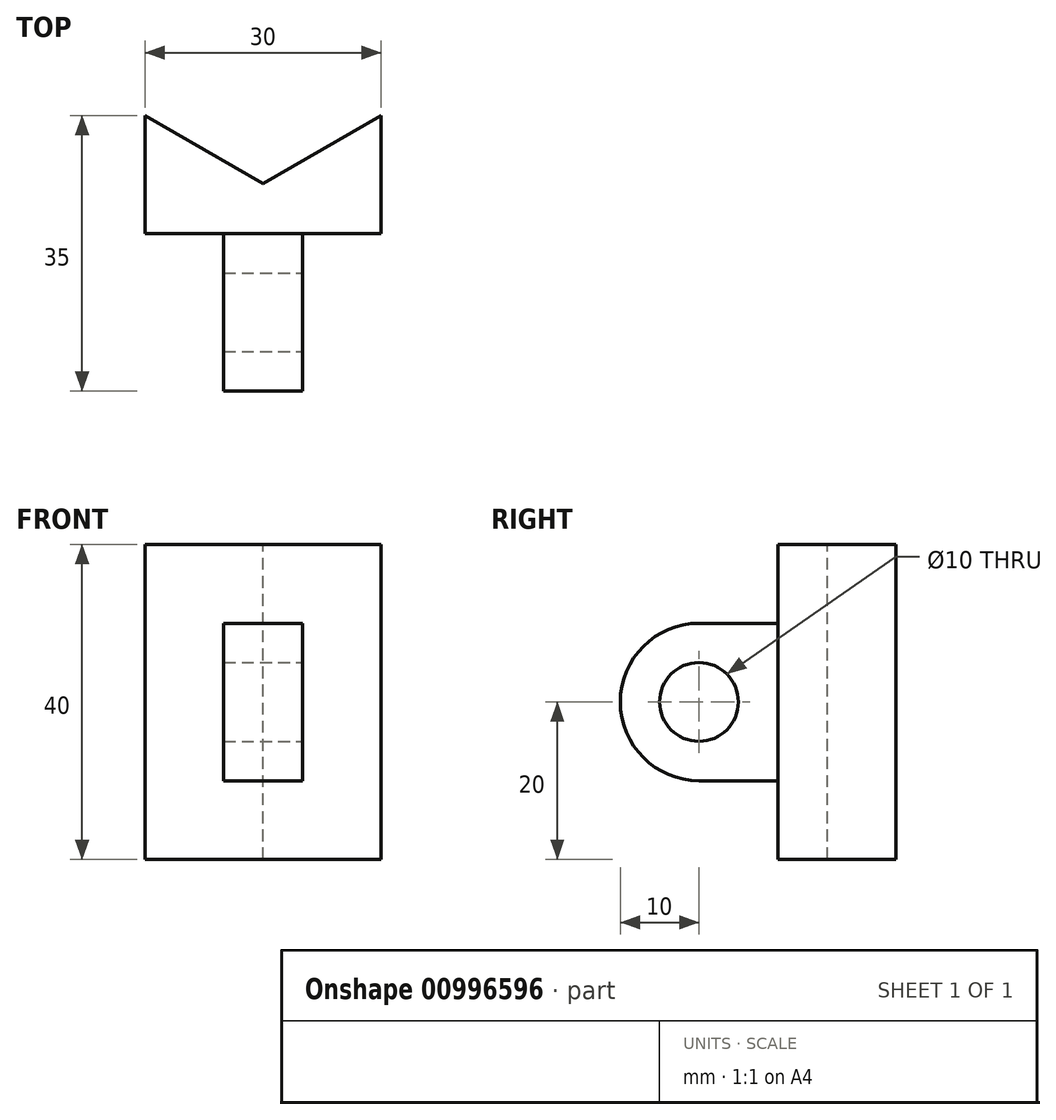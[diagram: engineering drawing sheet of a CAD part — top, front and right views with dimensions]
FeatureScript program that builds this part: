
annotation { "Feature Type Name" : "Feature", "Feature Type Description" : "" }
export const myFeature = defineFeature(function(context is Context, id is Id, definition is map)
    precondition{}
    {
        {
            var Q0;
            Q0=qCreatedBy(makeId("Front.planeOp"),FACE);
            var sketch = newSketch(context, id + "F0", { "sketchPlane" : qUnion([Q0])});
            skLineSegment(sketch, "E0.bottom", {"start": v(-15, 20) * mm, "end": v(15, 20) * mm});
            skLineSegment(sketch, "E0.top", {"start": v(-15, -20) * mm, "end": v(15, -20) * mm});
            skLineSegment(sketch, "E0.left", {"start": v(-15, 20) * mm, "end": v(-15, -20) * mm});
            skLineSegment(sketch, "E0.right", {"start": v(15, 20) * mm, "end": v(15, -20) * mm});
            skSolve(sketch);
        }
        {
            var Q0;
            Q0=makeQuery(id+"F0.imprint","IMPRINT",FACE,{"disambiguationData":[TD([[makeQuery(id+"F0.imprint","IMPRINT",EDGE,{"derivedFrom":sQuery(id+"F0.wireOp",EDGE,"E0.bottom")}),-1.0]])]});
            extrude(context, id + "F1", {"entities" : qUnion([Q0]), "depth" : 15 * mm, "offsetDistance" : 25 * mm});
        }
        {
            var Q0;
            Q0=makeQuery(id+"F1.opExtrude","CAP_FACE",FACE,{"disambiguationData":[OSD([sQuery(id+"F0.wireOp",EDGE,"E0.bottom"),sQuery(id+"F0.wireOp",EDGE,"E0.top"),sQuery(id+"F0.wireOp",EDGE,"E0.left"),sQuery(id+"F0.wireOp",EDGE,"E0.right")])],"isStart":false});
            var sketch = newSketch(context, id + "F2", { "sketchPlane" : qUnion([Q0])});
            skLineSegment(sketch, "E1.bottom", {"start": v(-5, 10) * mm, "end": v(5, 10) * mm});
            skLineSegment(sketch, "E1.top", {"start": v(-5, -10) * mm, "end": v(5, -10) * mm});
            skLineSegment(sketch, "E1.left", {"start": v(-5, 10) * mm, "end": v(-5, -10) * mm});
            skLineSegment(sketch, "E1.right", {"start": v(5, 10) * mm, "end": v(5, -10) * mm});
            skSolve(sketch);
        }
        {
            var Q0;
            Q0=makeQuery(id+"F2.imprint","IMPRINT",FACE,{"disambiguationData":[TD([[makeQuery(id+"F2.imprint","IMPRINT",EDGE,{"derivedFrom":sQuery(id+"F2.wireOp",EDGE,"E1.bottom")}),-1.0]])]});
            extrude(context, id + "F3", {"entities" : qUnion([Q0]), "operationType" : NewBodyOperationType.ADD, "depth" : 20 * mm, "offsetDistance" : 25 * mm});
        }
        {
            var Q0;
            Q0=makeQuery(id+"F3.opExtrude","SWEPT_FACE",FACE,{"disambiguationData":[OSD([sQuery(id+"F2.wireOp",EDGE,"E1.right")])]});
            var sketch = newSketch(context, id + "F4", { "sketchPlane" : qUnion([Q0])});
            skCircle(sketch, "E2", {"center": v(-25, 0) * mm, "radius": 5 * mm});
            skSolve(sketch);
        }
        {
            var Q0;
            Q0=makeQuery(id+"F4.imprint","IMPRINT",FACE,{"disambiguationData":[TD([[makeQuery(id+"F4.imprint","IMPRINT",EDGE,{"derivedFrom":sQuery(id+"F4.wireOp",EDGE,"E2")}),1.0]])]});
            extrude(context, id + "F5", {"entities" : qUnion([Q0]), "operationType" : NewBodyOperationType.REMOVE, "endBound" : BoundingType.THROUGH_ALL, "oppositeDirection" : true, "depth" : 25 * mm, "offsetDistance" : 25 * mm});
        }
        {
            var Q0;
            Q0=makeQuery(id+"F3.opExtrude","CAP_EDGE",EDGE,{"disambiguationData":[OSD([sQuery(id+"F2.wireOp",EDGE,"E1.bottom")])],"isStart":false});
            var Q1;
            Q1=makeQuery(id+"F3.opExtrude","CAP_EDGE",EDGE,{"disambiguationData":[OSD([sQuery(id+"F2.wireOp",EDGE,"E1.top")])],"isStart":false});
            fillet(context, id + "F6", {"entities" : qUnion([Q0, Q1]), "radius" : 10 * mm, "tangentPropagation" : true, "allowEdgeOverflow" : false});
        }
        {
            var Q0;
            Q0=makeQuery(id+"F1.opExtrude","SWEPT_FACE",FACE,{"disambiguationData":[OSD([sQuery(id+"F0.wireOp",EDGE,"E0.bottom")])]});
            var sketch = newSketch(context, id + "F7", { "sketchPlane" : qUnion([Q0])});
            skLineSegment(sketch, "E3", {"start": v(-15, 0) * mm, "end": v(0, -8.66) * mm});
            skLineSegment(sketch, "E4", {"start": v(0, -8.66) * mm, "end": v(15, 0) * mm});
            skSolve(sketch);
        }
        {
            var Q0;
            Q0=makeQuery(id+"F7.imprint","IMPRINT",FACE,{"disambiguationData":[TD([[makeQuery(id+"F7.imprint","IMPRINT",EDGE,{"derivedFrom":sQuery(id+"F7.wireOp",EDGE,"E3")}),1.0]])]});
            extrude(context, id + "F8", {"entities" : qUnion([Q0]), "operationType" : NewBodyOperationType.REMOVE, "endBound" : BoundingType.THROUGH_ALL, "oppositeDirection" : true, "depth" : 25 * mm, "offsetDistance" : 25 * mm});
        }
    });
